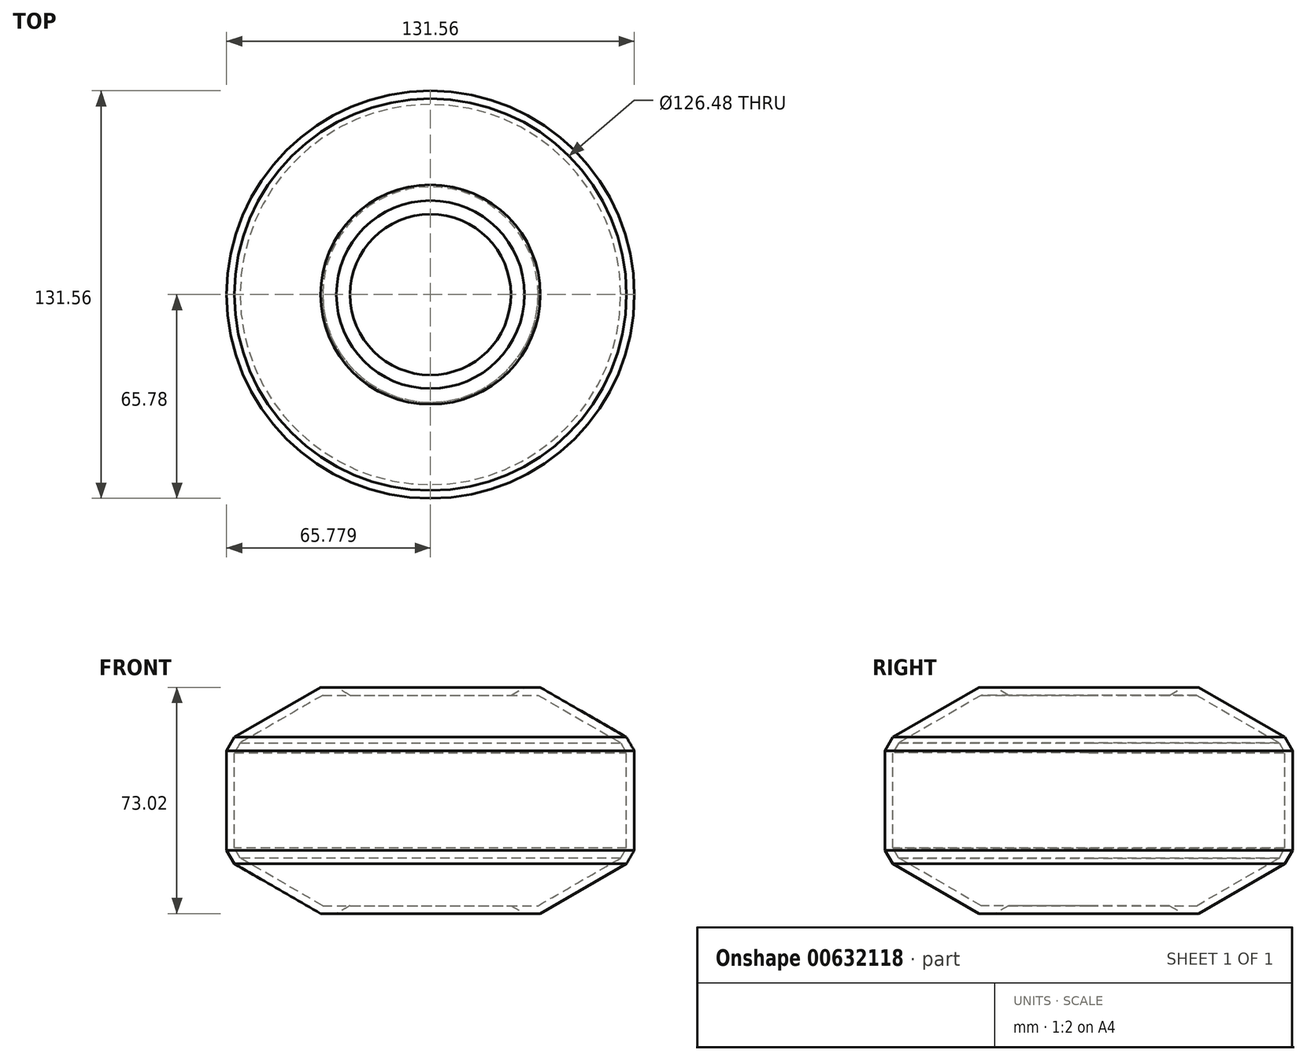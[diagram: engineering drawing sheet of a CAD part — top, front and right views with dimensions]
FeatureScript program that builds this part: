
annotation { "Feature Type Name" : "Feature", "Feature Type Description" : "" }
export const myFeature = defineFeature(function(context is Context, id is Id, definition is map)
    precondition{}
    {
        {
            var Q0;
            Q0=qCreatedBy(makeId("Front.planeOp"),FACE);
            var sketch = newSketch(context, id + "F0", { "sketchPlane" : qUnion([Q0])});
            skCircle(sketch, "E0.cCircle", {"center": v(0, 0) * mm, "radius": 32.89 * mm, "construction": true});
            skLineSegment(sketch, "E0.0", {"start": v(32.89, 18.99) * mm, "end": v(32.89, -18.99) * mm});
            skLineSegment(sketch, "E0.1", {"start": v(32.89, -18.99) * mm, "end": v(0, -37.98) * mm});
            skLineSegment(sketch, "E0.2", {"start": v(0, -37.98) * mm, "end": v(-32.89, -18.99) * mm});
            skLineSegment(sketch, "E0.3", {"start": v(-32.89, -18.99) * mm, "end": v(-32.89, 18.99) * mm});
            skLineSegment(sketch, "E0.4", {"start": v(-32.89, 18.99) * mm, "end": v(0, 37.98) * mm});
            skLineSegment(sketch, "E0.5", {"start": v(0, 37.98) * mm, "end": v(32.89, 18.99) * mm});
            skPoint(sketch, "E0.0.midPoint", {"position": v(32.89, 0) * mm});
            skLineSegment(sketch, "E1", {"start": v(0, 37.98) * mm, "end": v(0, 0) * mm});
            skLineSegment(sketch, "E2", {"start": v(0, 18.99) * mm, "end": v(32.89, 18.99) * mm});
            skLineSegment(sketch, "E3", {"start": v(0, 0) * mm, "end": v(32.89, -18.99) * mm});
            skLineSegment(sketch, "E4", {"start": v(0, 0) * mm, "end": v(-32.89, -18.99) * mm});
            skLineSegment(sketch, "E5", {"start": v(-16.44, -9.5) * mm, "end": v(-32.89, 18.99) * mm});
            skLineSegment(sketch, "E6", {"start": v(16.44, -9.5) * mm, "end": v(0, -37.98) * mm});
            skLineSegment(sketch, "E7", {"start": v(-16.44, -9.5) * mm, "end": v(0, -37.98) * mm});
            skLineSegment(sketch, "E8", {"start": v(16.44, -9.5) * mm, "end": v(32.89, 18.99) * mm});
            skLineSegment(sketch, "E9", {"start": v(0, 18.99) * mm, "end": v(-32.89, 18.99) * mm});
            skSolve(sketch);
        }
        {
            var Q0;
            {var subQ0=sQuery(id+"F0.wireOp",EDGE,"E0.0");Q0=makeQuery(id+"F0.imprint","IMPRINT",FACE,{"disambiguationData":[TD([[makeQuery(id+"F0.imprint","IMPRINT",EDGE,{"derivedFrom":subQ0}),-1.0]])]});}
            var Q1;
            {var subQ3=sQuery(id+"F0.wireOp",EDGE,"E2");Q1=makeQuery(id+"F0.imprint","IMPRINT",FACE,{"disambiguationData":[TD([[makeQuery(id+"F0.imprint","IMPRINT",EDGE,{"derivedFrom":subQ3}),-1.0]])]});}
            var Q2;
            {var subQ3=sQuery(id+"F0.wireOp",EDGE,"E6");Q2=makeQuery(id+"F0.imprint","IMPRINT",FACE,{"disambiguationData":[TD([[makeQuery(id+"F0.imprint","IMPRINT",EDGE,{"derivedFrom":subQ3}),-1.0]])]});}
            var Q3;
            {var subQ0=sQuery(id+"F0.wireOp",EDGE,"E0.5");Q3=makeQuery(id+"F0.imprint","IMPRINT",FACE,{"disambiguationData":[TD([[makeQuery(id+"F0.imprint","IMPRINT",EDGE,{"derivedFrom":subQ0}),-1.0]])]});}
            var Q4;
            {var subQ0=sQuery(id+"F0.wireOp",EDGE,"E0.4");Q4=makeQuery(id+"F0.imprint","IMPRINT",FACE,{"disambiguationData":[TD([[makeQuery(id+"F0.imprint","IMPRINT",EDGE,{"derivedFrom":subQ0}),-1.0]])]});}
            var Q5;
            {var subQ0=sQuery(id+"F0.wireOp",EDGE,"E0.2");Q5=makeQuery(id+"F0.imprint","IMPRINT",FACE,{"disambiguationData":[TD([[makeQuery(id+"F0.imprint","IMPRINT",EDGE,{"derivedFrom":subQ0}),-1.0]])]});}
            var Q6;
            {var subQ4=sQuery(id+"F0.wireOp",EDGE,"E5");Q6=makeQuery(id+"F0.imprint","IMPRINT",FACE,{"disambiguationData":[TD([[makeQuery(id+"F0.imprint","IMPRINT",EDGE,{"derivedFrom":subQ4}),-1.0]])]});}
            var Q7;
            {var subQ0=sQuery(id+"F0.wireOp",EDGE,"E0.3");Q7=makeQuery(id+"F0.imprint","IMPRINT",FACE,{"disambiguationData":[TD([[makeQuery(id+"F0.imprint","IMPRINT",EDGE,{"derivedFrom":subQ0}),-1.0]])]});}
            var Q8;
            {var subQ0=sQuery(id+"F0.wireOp",EDGE,"E0.1");Q8=makeQuery(id+"F0.imprint","IMPRINT",FACE,{"disambiguationData":[TD([[makeQuery(id+"F0.imprint","IMPRINT",EDGE,{"derivedFrom":subQ0}),-1.0]])]});}
            var Q9;
            Q9=sQuery(id+"F0.wireOp",EDGE,"E0.0");
            revolve(context, id + "F1", {"entities" : qUnion([Q0, Q1, Q2, Q3, Q4, Q5, Q6, Q7, Q8]), "axis" : qUnion([Q9]), "revolveType" : RevolveType.FULL});
        }
        {
            var Q0;
            Q0=makeQuery(id+"F1.opRevolve","SWEPT_FACE",FACE,{"disambiguationData":[OSD([sQuery(id+"F0.wireOp",EDGE,"E0.4")])]});
            var Q1;
            Q1=makeQuery(id+"F1.opRevolve","SWEPT_FACE",FACE,{"disambiguationData":[OSD([sQuery(id+"F0.wireOp",EDGE,"E0.2")])]});
            var Q2;
            Q2=makeQuery(id+"F1.opRevolve","SWEPT_FACE",FACE,{"disambiguationData":[OSD([sQuery(id+"F0.wireOp",EDGE,"E0.1")])]});
            chamfer(context, id + "F2", {"entities" : qUnion([Q0, Q1, Q2]), "width" : 5.08 * mm, "tangentPropagation" : true});
        }
        {
            var Q0;
            Q0=makeQuery(id+"F1.opRevolve","SWEPT_FACE",FACE,{"disambiguationData":[OSD([sQuery(id+"F0.wireOp",EDGE,"E0.5")])]});
            var Q1;
            Q1=makeQuery(id+"F1.opRevolve","SWEPT_FACE",FACE,{"disambiguationData":[OSD([sQuery(id+"F0.wireOp",EDGE,"E0.1")])]});
            shell(context, id + "F3", {"entities" : qUnion([Q0, Q1]), "thickness" : 2.54 * mm});
        }
    });
